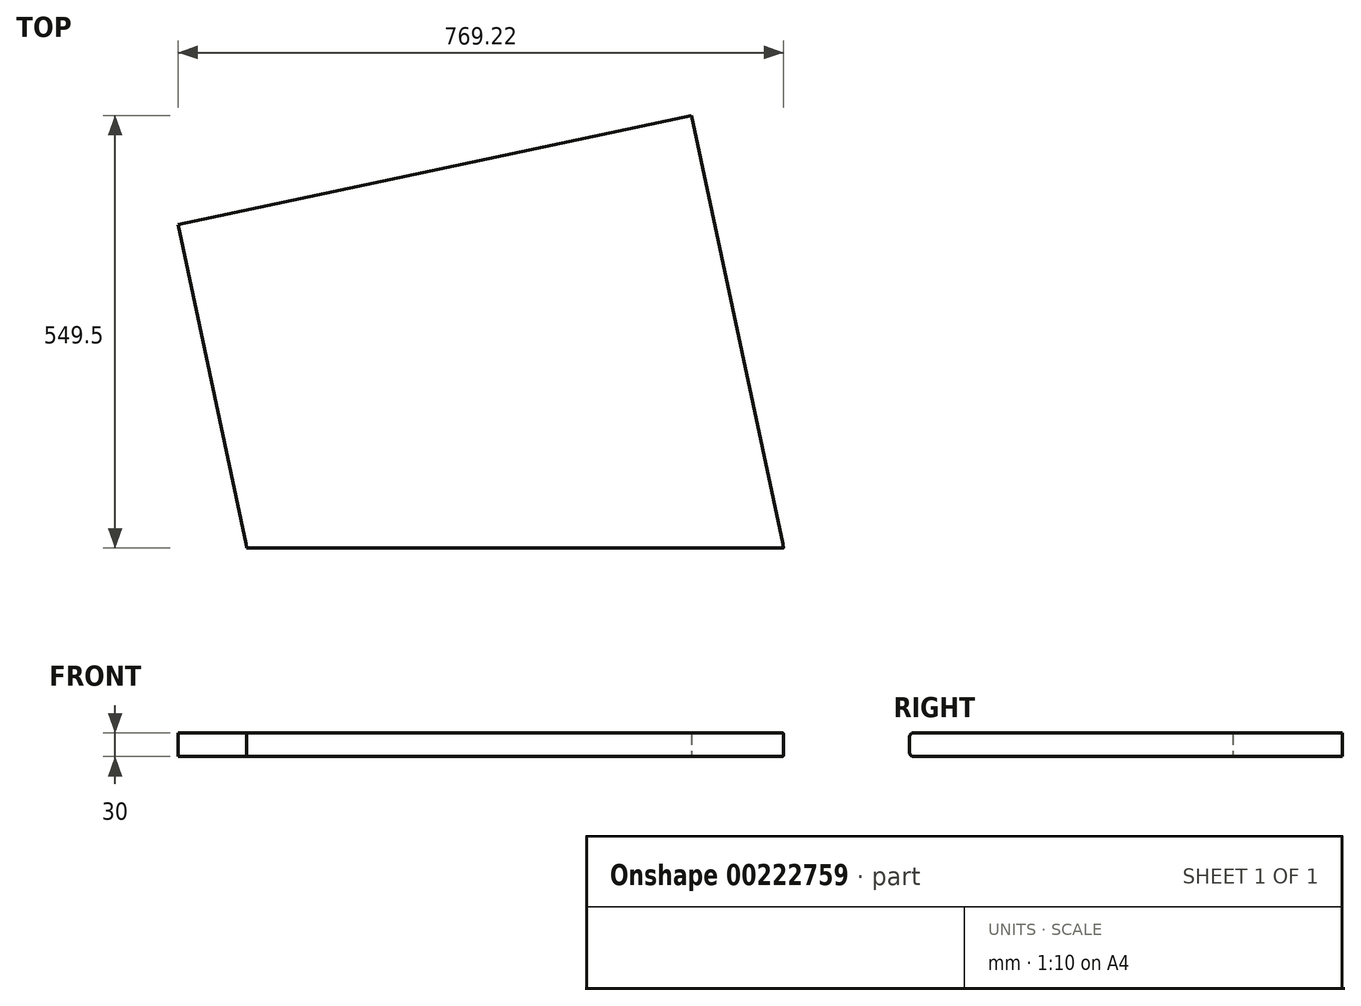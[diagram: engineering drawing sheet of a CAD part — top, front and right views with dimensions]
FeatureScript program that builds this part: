
annotation { "Feature Type Name" : "Feature", "Feature Type Description" : "" }
export const myFeature = defineFeature(function(context is Context, id is Id, definition is map)
    precondition{}
    {
        {
            var Q0;
            Q0=qCreatedBy(makeId("Right.planeOp"),FACE);
            var sketch = newSketch(context, id + "F0", { "sketchPlane" : qUnion([Q0])});
            skLineSegment(sketch, "E0.bottom", {"start": v(300, 15) * mm, "end": v(-295, 15) * mm});
            skLineSegment(sketch, "E0.top", {"start": v(300, -15) * mm, "end": v(-295, -15) * mm});
            skLineSegment(sketch, "E0.left", {"start": v(300, 15) * mm, "end": v(300, -15) * mm});
            skLineSegment(sketch, "E0.right", {"start": v(-300, 10) * mm, "end": v(-300, -10) * mm});
            skPoint(sketch, "E0.middle", {"position": v(0, 0) * mm});
            skPoint(sketch, "E1.visualSharp", {"position": v(-300, 15) * mm});
            skArc(sketch, "E1.filletArc", {"start": v(-295, 15) * mm, "mid": v(-298.54, 13.54) * mm, "end": v(-300, 10) * mm});
            skPoint(sketch, "E2.visualSharp", {"position": v(-300, -15) * mm});
            skArc(sketch, "E2.filletArc", {"start": v(-300, -10) * mm, "mid": v(-298.54, -13.54) * mm, "end": v(-295, -15) * mm});
            skSolve(sketch);
        }
        {
            var Q0;
            Q0=qCreatedBy(makeId("Top.planeOp"),FACE);
            var sketch = newSketch(context, id + "F1", { "sketchPlane" : qUnion([Q0])});
            skLineSegment(sketch, "E3.bottom", {"start": v(450, 300) * mm, "end": v(-450, 300) * mm, "construction": true});
            skLineSegment(sketch, "E3.top", {"start": v(450, -300) * mm, "end": v(-450, -300) * mm, "construction": true});
            skLineSegment(sketch, "E3.left", {"start": v(450, 300) * mm, "end": v(450, -300) * mm, "construction": true});
            skLineSegment(sketch, "E3.right", {"start": v(-450, 300) * mm, "end": v(-450, -300) * mm, "construction": true});
            skPoint(sketch, "E3.middle", {"position": v(0, 0) * mm});
            skLineSegment(sketch, "E4", {"start": v(0, 0) * mm, "end": v(450, 0) * mm, "construction": true});
            skLineSegment(sketch, "E5", {"start": v(450, 0) * mm, "end": v(450, 95.65) * mm, "construction": true});
            skLineSegment(sketch, "E6", {"start": v(450, 95.65) * mm, "end": v(0, 0) * mm, "construction": true});
            skLineSegment(sketch, "E7", {"start": v(0, 0) * mm, "end": v(-450, -95.65) * mm, "construction": true});
            skLineSegment(sketch, "E8", {"start": v(-450, -270) * mm, "end": v(450, -270) * mm, "construction": true});
            skLineSegment(sketch, "E9", {"start": v(450, -300) * mm, "end": v(322.47, 300) * mm, "construction": true});
            skLineSegment(sketch, "E10", {"start": v(-231.9, -300) * mm, "end": v(-450, 726.07) * mm, "construction": true});
            skPoint(sketch, "E11", {"position": v(-282.89, -60.13) * mm});
            skPoint(sketch, "E12", {"position": v(369.54, 78.55) * mm});
            skPoint(sketch, "E13", {"position": v(-238.28, -270) * mm});
            skLineSegment(sketch, "E14", {"start": v(-238.28, -270) * mm, "end": v(414.15, -131.32) * mm, "construction": true});
            skLineSegment(sketch, "E15", {"start": v(-319.22, 110.82) * mm, "end": v(333.2, 249.5) * mm, "construction": true});
            skPoint(sketch, "E16", {"position": v(443.62, -270) * mm});
            skLineSegment(sketch, "E17", {"start": v(-231.9, -300) * mm, "end": v(-189.97, -497.26) * mm, "construction": true});
            skLineSegment(sketch, "E18", {"start": v(450, -300) * mm, "end": v(462.45, -358.58) * mm, "construction": true});
            skLineSegment(sketch, "E19", {"start": v(-189.97, -497.26) * mm, "end": v(462.45, -358.58) * mm, "construction": true});
            skLineSegment(sketch, "E20", {"start": v(-189.97, -497.26) * mm, "end": v(-319.22, 110.82) * mm});
            skLineSegment(sketch, "E21", {"start": v(-319.22, 110.82) * mm, "end": v(333.2, 249.5) * mm});
            skLineSegment(sketch, "E22", {"start": v(333.2, 249.5) * mm, "end": v(462.45, -358.58) * mm});
            skLineSegment(sketch, "E23", {"start": v(462.45, -358.58) * mm, "end": v(-189.97, -497.26) * mm});
            skPoint(sketch, "E24", {"position": v(-359.44, 300) * mm});
            skSolve(sketch);
        }
        {
            var Q0;
            Q0=makeQuery(id+"F0.imprint","IMPRINT",FACE,{"disambiguationData":[TD([[makeQuery(id+"F0.imprint","IMPRINT",EDGE,{"derivedFrom":sQuery(id+"F0.wireOp",EDGE,"E0.bottom")}),1.0]])]});
            extrude(context, id + "F2", {"entities" : qUnion([Q0]), "endBound" : BoundingType.SYMMETRIC, "depth" : 1000 * mm});
        }
        {
            var Q0;
            Q0=makeQuery(id+"F1.imprint","IMPRINT",FACE,{"disambiguationData":[TD([[makeQuery(id+"F1.imprint","IMPRINT",EDGE,{"derivedFrom":sQuery(id+"F1.wireOp",EDGE,"E20")}),-1.0]])]});
            extrude(context, id + "F3", {"entities" : qUnion([Q0]), "operationType" : NewBodyOperationType.INTERSECT, "endBound" : BoundingType.SYMMETRIC, "depth" : 100 * mm});
        }
    });
